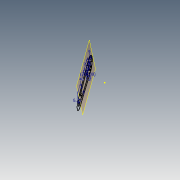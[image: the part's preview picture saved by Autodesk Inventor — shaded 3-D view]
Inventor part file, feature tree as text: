
AUTODESK INVENTOR PART (.ipt)
format: ipt  version: 2014 SP1 (Build 180222100, 222)  size: 133,120 bytes
history: native  units: in
note: dims shown in document units (in); Inventor stores cm internally (conversion verified against a paired STEP export)
features: plane x1, extrude x1, sketch x1
ambient origin geometry x8: Origin, YZ Plane, XZ Plane, XY Plane, X Axis, Y Axis, Z Axis, Center Point
bodies: Solid1 (feature_tree)
feature tree (3):
  plane  "Work Plane3"
  extrude  "Extrusion1"  Depth=0.2228in
  sketch  "Sketch1"  dims[d0=1.5748in d1=0.3543in d2=0.0512in d3=0.2894in d4=0.0512in d5=0.0512in d6=0.25in d7=0.1575in d8=0.1575in d9=0.1575in d10=0.0787in d11=1.5748in d13=360.0deg d15=0.2228in d16=0.0in]
